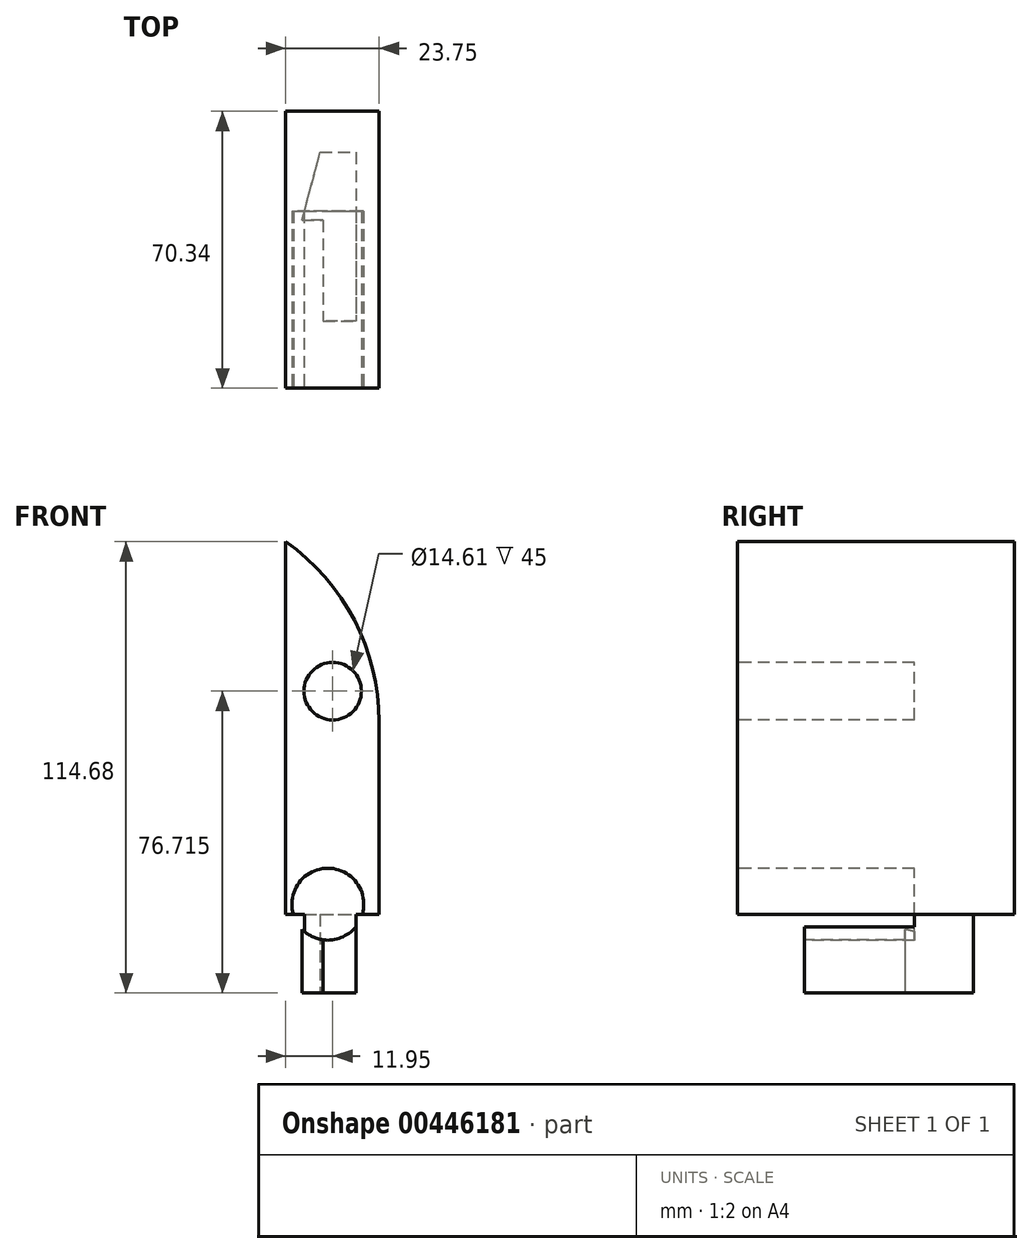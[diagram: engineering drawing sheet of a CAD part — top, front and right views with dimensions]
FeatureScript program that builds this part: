
annotation { "Feature Type Name" : "Feature", "Feature Type Description" : "" }
export const myFeature = defineFeature(function(context is Context, id is Id, definition is map)
    precondition{}
    {
        {
            var Q0;
            Q0=qCreatedBy(makeId("Front.planeOp"),FACE);
            var sketch = newSketch(context, id + "F0", { "sketchPlane" : qUnion([Q0])});
            skLineSegment(sketch, "E0", {"start": v(-59.91, 66.38) * mm, "end": v(-59.91, -48.3) * mm});
            skLineSegment(sketch, "E1", {"start": v(-59.91, -48.3) * mm, "end": v(-36.16, -48.3) * mm});
            skLineSegment(sketch, "E2", {"start": v(-36.16, -48.3) * mm, "end": v(-36.16, 20.68) * mm});
            skArc(sketch, "E3", {"start": v(-36.16, 20.68) * mm, "mid": v(-42.46, 46.43) * mm, "end": v(-59.91, 66.38) * mm});
            skSolve(sketch);
        }
        {
            var Q0;
            Q0 = qSketchRegion(id + "F0", true);
            extrude(context, id + "F1", {"entities" : qUnion([Q0]), "depth" : 70.34 * mm});
        }
        {
            var Q0;
            Q0=makeQuery(id+"F1.opExtrude","CAP_FACE",FACE,{"disambiguationData":[OSD([sQuery(id+"F0.wireOp",EDGE,"E0"),sQuery(id+"F0.wireOp",EDGE,"E1"),sQuery(id+"F0.wireOp",EDGE,"E2"),sQuery(id+"F0.wireOp",EDGE,"E3")])],"isStart":false});
            var sketch = newSketch(context, id + "F2", { "sketchPlane" : qUnion([Q0])});
            skSolve(sketch);
        }
        {
            var Q0;
            Q0=makeQuery(id+"F2.imprint","IMPRINT",FACE,{"disambiguationData":[TD([[makeQuery(id+"F2.imprint","IMPRINT",EDGE,{"derivedFrom":makeQuery(id+"F1.opExtrude","CAP_EDGE",EDGE,{"disambiguationData":[OSD([sQuery(id+"F0.wireOp",EDGE,"E0")])],"isStart":false})}),1.0]])]});
            var sketch = newSketch(context, id + "F3", { "sketchPlane" : qUnion([Q0])});
            skCircle(sketch, "E4", {"center": v(-47.96, 28.42) * mm, "radius": 7.3 * mm});
            skCircle(sketch, "E5", {"center": v(-49.19, -25.72) * mm, "radius": 9.14 * mm});
            skSolve(sketch);
        }
        {
            var Q0;
            Q0 = qSketchRegion(id + "F3", true);
            extrude(context, id + "F4", {"entities" : qUnion([Q0]), "operationType" : NewBodyOperationType.REMOVE, "oppositeDirection" : true, "depth" : 45 * mm});
        }
        {
            var Q0;
            Q0=makeQuery(id+"F1.opExtrude","SWEPT_FACE",FACE,{"disambiguationData":[OSD([sQuery(id+"F0.wireOp",EDGE,"E1")])]});
            var sketch = newSketch(context, id + "F5", { "sketchPlane" : qUnion([Q0])});
            skLineSegment(sketch, "E6", {"start": v(-51.15, 10.42) * mm, "end": v(-42.07, 10.42) * mm});
            skLineSegment(sketch, "E7", {"start": v(-42.07, 10.42) * mm, "end": v(-42.07, 53.33) * mm});
            skLineSegment(sketch, "E8", {"start": v(-42.07, 53.33) * mm, "end": v(-50.4, 53.33) * mm});
            skLineSegment(sketch, "E9", {"start": v(-50.4, 27.69) * mm, "end": v(-50.4, 53.33) * mm});
            skLineSegment(sketch, "E10", {"start": v(-55.74, 27.69) * mm, "end": v(-50.4, 27.69) * mm});
            skLineSegment(sketch, "E11", {"start": v(-55.74, 27.69) * mm, "end": v(-51.15, 10.42) * mm});
            skSolve(sketch);
        }
        {
            var Q0;
            Q0=makeQuery(id+"F5.imprint","IMPRINT",FACE,{"disambiguationData":[TD([[makeQuery(id+"F5.imprint","IMPRINT",EDGE,{"derivedFrom":sQuery(id+"F5.wireOp",EDGE,"E6")}),-1.0]])]});
            extrude(context, id + "F6", {"entities" : qUnion([Q0]), "operationType" : NewBodyOperationType.REMOVE, "oppositeDirection" : true, "depth" : 20 * mm});
        }
    });
